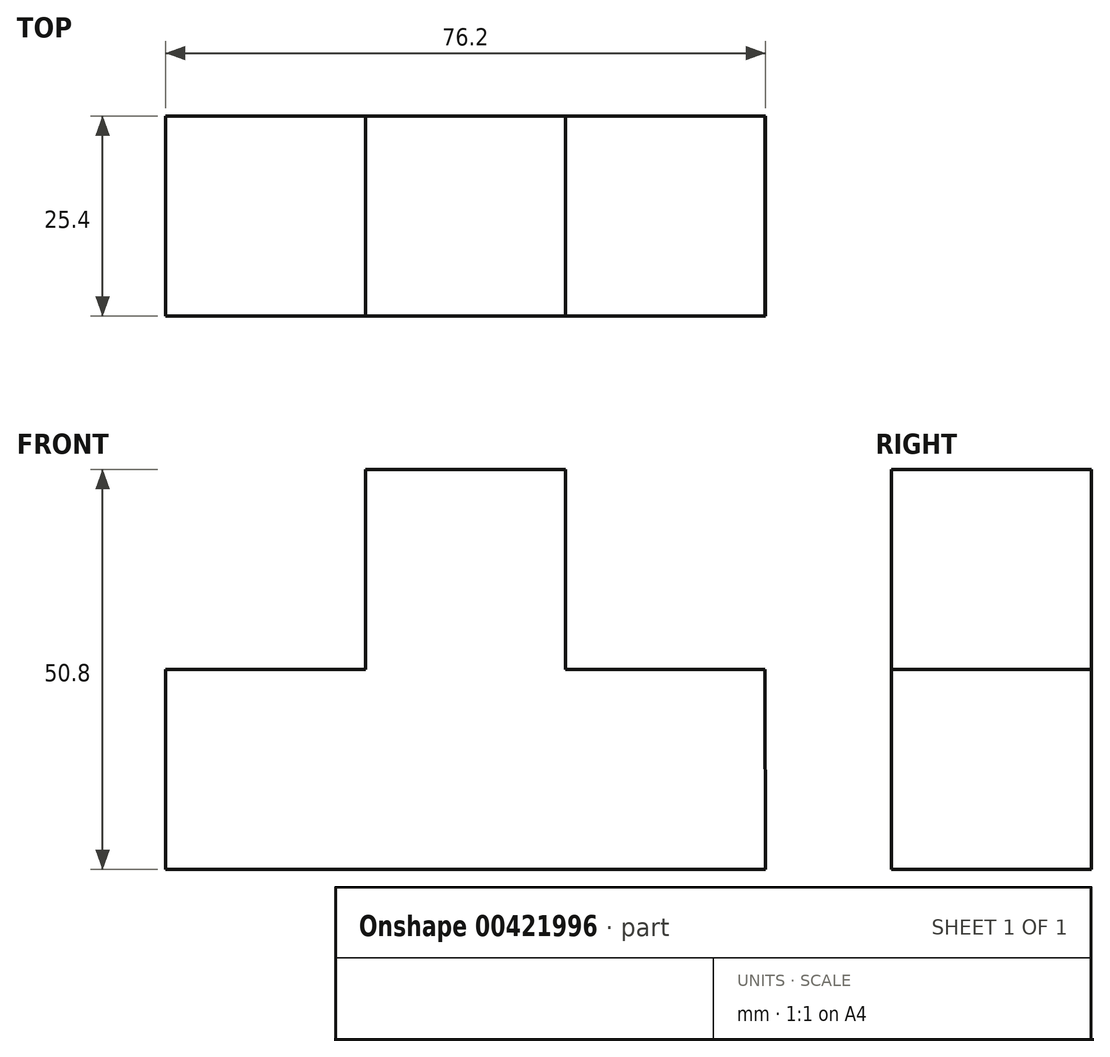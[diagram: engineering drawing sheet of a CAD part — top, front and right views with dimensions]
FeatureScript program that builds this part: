
annotation { "Feature Type Name" : "Feature", "Feature Type Description" : "" }
export const myFeature = defineFeature(function(context is Context, id is Id, definition is map)
    precondition{}
    {
        {
            var Q0;
            Q0=qCreatedBy(makeId("Front.planeOp"),FACE);
            var sketch = newSketch(context, id + "F0", { "sketchPlane" : qUnion([Q0])});
            skLineSegment(sketch, "E0", {"start": v(0.05, 0) * mm, "end": v(-76.15, 0) * mm});
            skLineSegment(sketch, "E1", {"start": v(-76.15, 0) * mm, "end": v(-76.15, 25.4) * mm});
            skLineSegment(sketch, "E2", {"start": v(-76.15, 25.4) * mm, "end": v(-50.75, 25.4) * mm});
            skLineSegment(sketch, "E3", {"start": v(-50.75, 25.4) * mm, "end": v(-50.75, 50.8) * mm});
            skLineSegment(sketch, "E4", {"start": v(-50.75, 50.8) * mm, "end": v(-25.35, 50.8) * mm});
            skLineSegment(sketch, "E5", {"start": v(-25.35, 50.8) * mm, "end": v(-25.35, 25.4) * mm});
            skLineSegment(sketch, "E6", {"start": v(-25.35, 25.4) * mm, "end": v(0, 25.4) * mm});
            skLineSegment(sketch, "E7", {"start": v(0, 25.4) * mm, "end": v(0.05, 0) * mm});
            skSolve(sketch);
        }
        {
            var Q0;
            Q0=makeQuery(id+"F0.imprint","IMPRINT",FACE,{"disambiguationData":[TD([[makeQuery(id+"F0.imprint","IMPRINT",EDGE,{"derivedFrom":sQuery(id+"F0.wireOp",EDGE,"E0")}),-1.0]])]});
            extrude(context, id + "F1", {"entities" : qUnion([Q0]), "depth" : 25.4 * mm});
        }
    });
